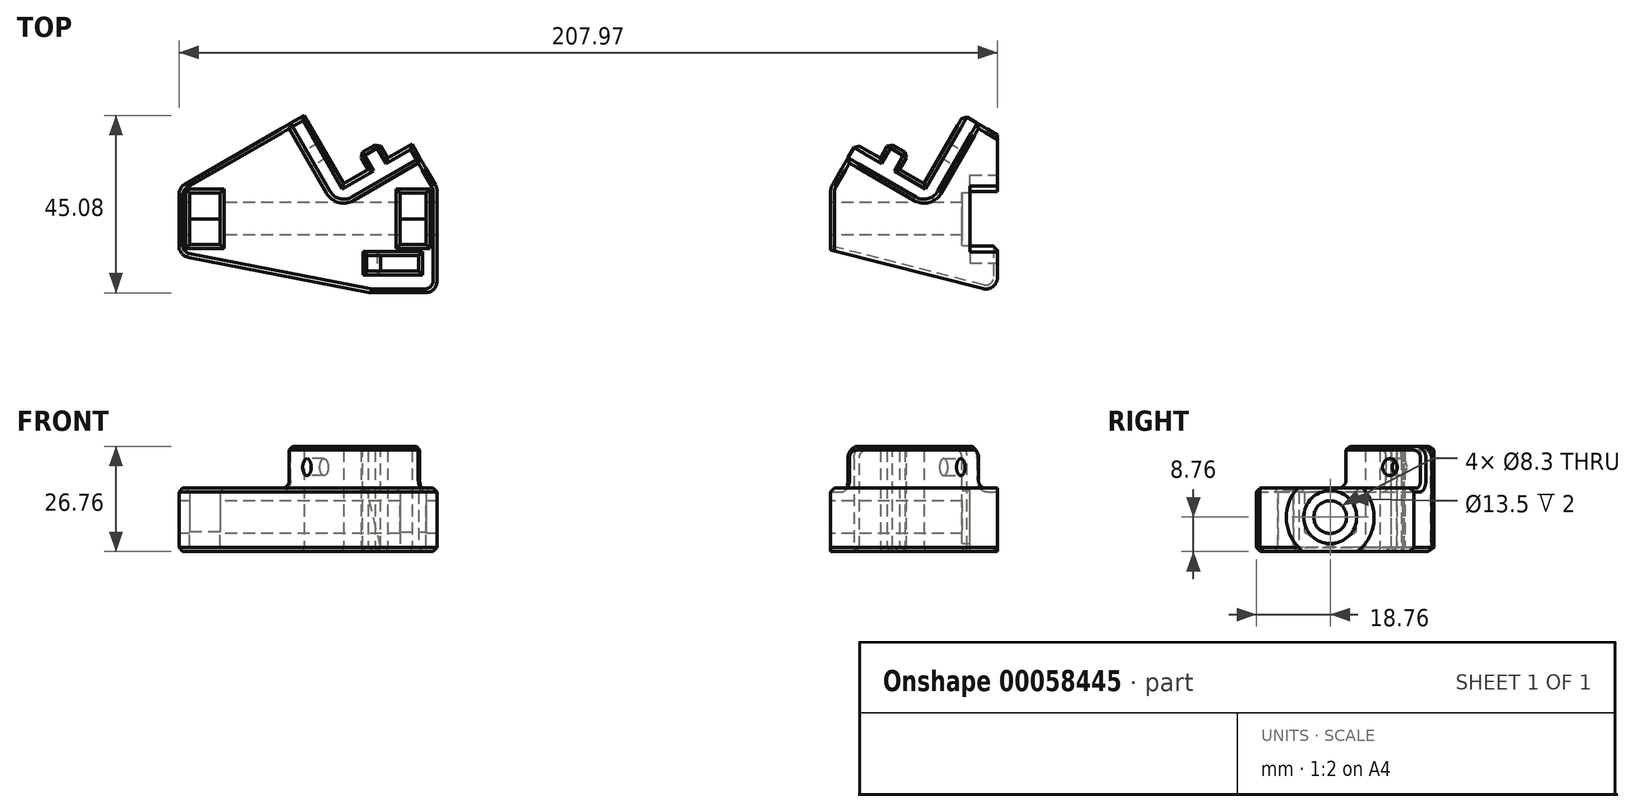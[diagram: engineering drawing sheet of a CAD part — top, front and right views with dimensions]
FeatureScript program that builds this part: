
annotation { "Feature Type Name" : "Feature", "Feature Type Description" : "" }
export const myFeature = defineFeature(function(context is Context, id is Id, definition is map)
    precondition{}
    {
        {
            assignVariable(context, id + "F0", {"name" : "line_width", "anyValue" : 0.48});
        }
        {
            assignVariable(context, id + "F1", {"name" : "tolerance", "anyValue" : 0.3});
        }
        {
            assignVariable(context, id + "F2", {"name" : "min_wall", "anyValue" : 3 * getVariable(context, 'line_width') * 0.95});
        }
        {
            assignVariable(context, id + "F3", {"name" : "M8_nut", "anyValue" : 12.8});
        }
        {
            assignVariable(context, id + "F4", {"name" : "M8_nut_long", "anyValue" : getVariable(context, 'M8_nut') / cos(30 * degree)});
        }
        {
            assignVariable(context, id + "F5", {"name" : "M8_nut_thickness", "anyValue" : 6.4});
        }
        {
            assignVariable(context, id + "F6", {"name" : "caliper_thickness", "anyValue" : 3.7});
        }
        {
            var Q0;
            Q0=qCreatedBy(makeId("Top.planeOp"),FACE);
            var sketch = newSketch(context, id + "F7", { "sketchPlane" : qUnion([Q0])});
            skLineSegment(sketch, "E0", {"start": v(-10, 26.32) * mm, "end": v(0, 9) * mm});
            skLineSegment(sketch, "E1", {"start": v(0, 9) * mm, "end": v(6.2, 12.57) * mm});
            skLineSegment(sketch, "E2", {"start": v(6.2, 12.57) * mm, "end": v(3.94, 16.47) * mm});
            skLineSegment(sketch, "E3", {"start": v(3.94, 16.47) * mm, "end": v(8.88, 19.32) * mm});
            skLineSegment(sketch, "E4", {"start": v(8.88, 19.32) * mm, "end": v(11.13, 15.42) * mm});
            skLineSegment(sketch, "E5", {"start": v(11.13, 15.42) * mm, "end": v(17.32, 19) * mm});
            skLineSegment(sketch, "E6", {"start": v(-41.87, 0) * mm, "end": v(23.72, 0) * mm, "construction": true});
            skLineSegment(sketch, "E7", {"start": v(-41.87, 0) * mm, "end": v(-41.87, -9.29) * mm});
            skLineSegment(sketch, "E8", {"start": v(-41.87, -9.29) * mm, "end": v(23.72, -9.29) * mm, "construction": true});
            skLineSegment(sketch, "E9", {"start": v(23.72, -9.29) * mm, "end": v(23.72, 0) * mm});
            skLineSegment(sketch, "E10", {"start": v(23.72, 0) * mm, "end": v(23.72, 7.92) * mm});
            skLineSegment(sketch, "E11", {"start": v(23.72, 7.92) * mm, "end": v(19.82, 14.67) * mm});
            skLineSegment(sketch, "E12", {"start": v(-41.87, 0) * mm, "end": v(-41.87, 7.92) * mm});
            skLineSegment(sketch, "E13", {"start": v(-41.87, 7.92) * mm, "end": v(-14.33, 23.82) * mm});
            skLineSegment(sketch, "E14", {"start": v(-41.87, -4) * mm, "end": v(23.72, -4) * mm, "construction": true});
            skLineSegment(sketch, "E15.MirrorCS", {"start": v(-41.87, 4) * mm, "end": v(23.72, 4) * mm, "construction": true});
            skLineSegment(sketch, "E16.rect.bottom", {"start": v(-31.44, -6.55) * mm, "end": v(-39.14, -6.55) * mm});
            skLineSegment(sketch, "E16.rect.top", {"start": v(-31.44, 6.55) * mm, "end": v(-39.14, 6.55) * mm});
            skLineSegment(sketch, "E16.rect.left", {"start": v(-31.44, -6.55) * mm, "end": v(-31.44, 6.55) * mm});
            skLineSegment(sketch, "E16.rect.right", {"start": v(-39.14, -6.55) * mm, "end": v(-39.14, 6.55) * mm});
            skPoint(sketch, "E16.rect.middle", {"position": v(-35.29, 0) * mm});
            skLineSegment(sketch, "E17.rect.bottom", {"start": v(20.98, -6.55) * mm, "end": v(14.28, -6.55) * mm});
            skLineSegment(sketch, "E17.rect.top", {"start": v(20.98, 6.55) * mm, "end": v(14.28, 6.55) * mm});
            skLineSegment(sketch, "E17.rect.left", {"start": v(20.98, -6.55) * mm, "end": v(20.98, 6.55) * mm});
            skLineSegment(sketch, "E17.rect.right", {"start": v(14.28, -6.55) * mm, "end": v(14.28, 6.55) * mm});
            skPoint(sketch, "E17.rect.middle", {"position": v(17.63, 0) * mm});
            skLineSegment(sketch, "E18", {"start": v(-39.14, -6.55) * mm, "end": v(-41.87, -6.55) * mm, "construction": true});
            skLineSegment(sketch, "E19", {"start": v(20.98, -6.55) * mm, "end": v(23.72, -6.55) * mm, "construction": true});
            skLineSegment(sketch, "E20", {"start": v(19.82, 14.67) * mm, "end": v(2.5, 4.67) * mm});
            skLineSegment(sketch, "E21", {"start": v(-4.33, 6.5) * mm, "end": v(-14.33, 23.82) * mm});
            skLineSegment(sketch, "E22", {"start": v(-14.33, 23.82) * mm, "end": v(-10, 26.32) * mm});
            skLineSegment(sketch, "E23", {"start": v(19.82, 14.67) * mm, "end": v(17.32, 19) * mm});
            skPoint(sketch, "E24.visualSharp", {"position": v(-1.83, 2.17) * mm});
            skArc(sketch, "E24.filletArc", {"start": v(-4.33, 6.5) * mm, "mid": v(-1.3, 4.17) * mm, "end": v(2.5, 4.67) * mm});
            skLineSegment(sketch, "E25", {"start": v(23.72, -9.29) * mm, "end": v(23.72, -18.76) * mm});
            skLineSegment(sketch, "E26", {"start": v(23.72, -18.76) * mm, "end": v(6.61, -18.76) * mm});
            skLineSegment(sketch, "E27", {"start": v(6.61, -18.76) * mm, "end": v(-41.87, -9.29) * mm});
            skSolve(sketch);
        }
        {
            var Q0;
            Q0 = qSketchRegion(id + "F7", true);
            extrude(context, id + "F8", {"entities" : qUnion([Q0]), "depth" : (getVariable(context, 'M8_nut_long') / 2) * mm});
        }
        {
            var Q0;
            Q0=makeQuery(id+"F7.imprint","IMPRINT",FACE,{"disambiguationData":[TD([[makeQuery(id+"F7.imprint","IMPRINT",EDGE,{"derivedFrom":sQuery(id+"F7.wireOp",EDGE,"E0")}),-1.0]])]});
            extrude(context, id + "F9", {"entities" : qUnion([Q0]), "operationType" : NewBodyOperationType.ADD, "depth" : 18 * mm});
        }
        {
            var Q0;
            Q0=makeQuery(id+"F7.imprint","IMPRINT",FACE,{"disambiguationData":[TD([[makeQuery(id+"F7.imprint","IMPRINT",EDGE,{"derivedFrom":sQuery(id+"F7.wireOp",EDGE,"E16.rect.bottom")}),-1.0]])]});
            var Q1;
            Q1=makeQuery(id+"F7.imprint","IMPRINT",FACE,{"disambiguationData":[TD([[makeQuery(id+"F7.imprint","IMPRINT",EDGE,{"derivedFrom":sQuery(id+"F7.wireOp",EDGE,"E17.rect.bottom")}),-1.0]])]});
            var Q2;
            Q2=makeQuery(id+"F7.imprint","IMPRINT",FACE,{"disambiguationData":[TD([[makeQuery(id+"F7.imprint","IMPRINT",EDGE,{"derivedFrom":sQuery(id+"F7.wireOp",EDGE,"E0")}),-1.0]])]});
            var Q3;
            Q3=makeQuery(id+"F7.imprint","IMPRINT",FACE,{"disambiguationData":[TD([[makeQuery(id+"F7.imprint","IMPRINT",EDGE,{"derivedFrom":sQuery(id+"F7.wireOp",EDGE,"E7")}),1.0]])]});
            extrude(context, id + "F10", {"entities" : qUnion([Q0, Q1, Q2, Q3]), "operationType" : NewBodyOperationType.ADD, "oppositeDirection" : true, "depth" : (getVariable(context, 'M8_nut_long') / 2 + getVariable(context, 'min_wall')) * mm});
        }
        {
            var Q0;
            Q0=makeQuery(id+"F8.opExtrude","SWEPT_FACE",FACE,{"disambiguationData":[OSD([sQuery(id+"F7.wireOp",EDGE,"E16.rect.right")])]});
            var sketch = newSketch(context, id + "F11", { "sketchPlane" : qUnion([Q0])});
            skCircle(sketch, "E28.cCircle", {"center": v(0, 0) * mm, "radius": 6.55 * mm, "construction": true});
            skPoint(sketch, "E28.cCircle.perimeterSnap0", {"position": v(0, 0) * mm});
            skLineSegment(sketch, "E28.0", {"start": v(6.55, 3.78) * mm, "end": v(6.55, -3.78) * mm});
            skLineSegment(sketch, "E28.1", {"start": v(6.55, -3.78) * mm, "end": v(0, -7.56) * mm});
            skLineSegment(sketch, "E28.2", {"start": v(0, -7.56) * mm, "end": v(-6.55, -3.78) * mm});
            skLineSegment(sketch, "E28.3", {"start": v(-6.55, -3.78) * mm, "end": v(-6.55, 3.78) * mm});
            skLineSegment(sketch, "E28.4", {"start": v(-6.55, 3.78) * mm, "end": v(0, 7.56) * mm});
            skLineSegment(sketch, "E28.5", {"start": v(0, 7.56) * mm, "end": v(6.55, 3.78) * mm});
            skPoint(sketch, "E28.0.midPoint", {"position": v(6.55, 0) * mm});
            skPoint(sketch, "E28.0.midPoint.positionSnap0", {"position": v(0, 0) * mm});
            skSolve(sketch);
        }
        {
            var Q0;
            {var subQ0=sQuery(id+"F7.wireOp",EDGE,"E25");var subQ1=sQuery(id+"F7.wireOp",EDGE,"E10");var subQ2=sQuery(id+"F7.wireOp",EDGE,"E9");Q0=makeQuery(id+"F10.boolean.opBoolean","MERGE",FACE,{"derivedFrom":[makeQuery(id+"F8.opExtrude","SWEPT_FACE",FACE,{"disambiguationData":[OSD([subQ2,subQ1,subQ0])]}),makeQuery(id+"F10.opExtrude","SWEPT_FACE",FACE,{"disambiguationData":[OSD([subQ2,subQ1,subQ0])]})]});}
            cPlane(context, id + "F12", {"entities" : qUnion([Q0]), "cplaneType" : CPlaneType.OFFSET, "offset" : 50 * mm, "width" : 150 * mm, "height" : 150 * mm});
        }
        {
            var Q0;
            Q0 = qSketchRegion(id + "F11", true);
            var Q1;
            Q1=makeQuery(id+"F8.opExtrude","SWEPT_FACE",FACE,{"disambiguationData":[OSD([sQuery(id+"F7.wireOp",EDGE,"E16.rect.left")])]});
            extrude(context, id + "F13", {"entities" : qUnion([Q0]), "operationType" : NewBodyOperationType.REMOVE, "endBound" : BoundingType.UP_TO_SURFACE, "endBoundEntityFace" : qUnion([Q1]), "depth" : (6.4 + getVariable(context, 'tolerance')) * mm});
        }
        {
            var Q0;
            Q0=makeQuery(id+"F8.opExtrude","SWEPT_FACE",FACE,{"disambiguationData":[OSD([sQuery(id+"F7.wireOp",EDGE,"E17.rect.left")])]});
            var sketch = newSketch(context, id + "F14", { "sketchPlane" : qUnion([Q0])});
            skCircle(sketch, "E29.cCircle", {"center": v(0, 0) * mm, "radius": 6.55 * mm, "construction": true});
            skPoint(sketch, "E29.cCircle.perimeterSnap0", {"position": v(0, 0) * mm});
            skLineSegment(sketch, "E29.0", {"start": v(6.55, 3.78) * mm, "end": v(6.55, -3.78) * mm});
            skLineSegment(sketch, "E29.1", {"start": v(6.55, -3.78) * mm, "end": v(0, -7.56) * mm});
            skLineSegment(sketch, "E29.2", {"start": v(0, -7.56) * mm, "end": v(-6.55, -3.78) * mm});
            skLineSegment(sketch, "E29.3", {"start": v(-6.55, -3.78) * mm, "end": v(-6.55, 3.78) * mm});
            skLineSegment(sketch, "E29.4", {"start": v(-6.55, 3.78) * mm, "end": v(0, 7.56) * mm});
            skLineSegment(sketch, "E29.5", {"start": v(0, 7.56) * mm, "end": v(6.55, 3.78) * mm});
            skPoint(sketch, "E29.0.midPoint", {"position": v(6.55, 0) * mm});
            skPoint(sketch, "E29.0.midPoint.positionSnap0", {"position": v(0, 0) * mm});
            skSolve(sketch);
        }
        {
            var Q0;
            Q0 = qSketchRegion(id + "F14", true);
            var Q1;
            Q1=makeQuery(id+"F8.opExtrude","SWEPT_FACE",FACE,{"disambiguationData":[OSD([sQuery(id+"F7.wireOp",EDGE,"E17.rect.right")])]});
            extrude(context, id + "F15", {"entities" : qUnion([Q0]), "operationType" : NewBodyOperationType.REMOVE, "endBound" : BoundingType.UP_TO_SURFACE, "endBoundEntityFace" : qUnion([Q1]), "depth" : (getVariable(context, 'M8_nut_thickness') + getVariable(context, 'tolerance')) * mm});
        }
        {
            var Q0;
            {var subQ0=sQuery(id+"F7.wireOp",EDGE,"E12");var subQ1=sQuery(id+"F7.wireOp",EDGE,"E7");Q0=makeQuery(id+"F10.boolean.opBoolean","MERGE",FACE,{"derivedFrom":[makeQuery(id+"F8.opExtrude","SWEPT_FACE",FACE,{"disambiguationData":[OSD([subQ1,subQ0])]}),makeQuery(id+"F10.opExtrude","SWEPT_FACE",FACE,{"disambiguationData":[OSD([subQ1,subQ0])]})]});}
            var sketch = newSketch(context, id + "F16", { "sketchPlane" : qUnion([Q0])});
            skCircle(sketch, "E30", {"center": v(0, 0) * mm, "radius": 4.15 * mm});
            skSolve(sketch);
        }
        {
            var Q0;
            {var subQ0=sQuery(id+"F7.wireOp",EDGE,"E22");var subQ4=sQuery(id+"F7.wireOp",EDGE,"E21");Q0=makeQuery(id+"F9.boolean.opBoolean","SPLIT",FACE,{"disambiguationData":[TD([makeQuery(id+"F9.opExtrude","SWEPT_FACE",FACE,{"disambiguationData":[OSD([subQ0])]})])],"derivedFrom":makeQuery(id+"F9.opExtrude","SWEPT_FACE",FACE,{"disambiguationData":[OSD([subQ4])]})});}
            var sketch = newSketch(context, id + "F17", { "sketchPlane" : qUnion([Q0])});
            skCircle(sketch, "E31", {"center": v(-17.8, 12.7) * mm, "radius": 2.15 * mm});
            skPoint(sketch, "E31.centerSnap0", {"position": v(-17.8, 18) * mm});
            skPoint(sketch, "E31.centerSnap1", {"position": v(-27.8, 12.7) * mm});
            skSolve(sketch);
        }
        {
            var Q0;
            Q0=makeQuery(id+"F17.imprint","IMPRINT",FACE,{"disambiguationData":[TD([[makeQuery(id+"F17.imprint","IMPRINT",EDGE,{"derivedFrom":sQuery(id+"F17.wireOp",EDGE,"E31")}),1.0]])]});
            var Q1;
            {var subQ0=sQuery(id+"F7.wireOp",EDGE,"E0");Q1=makeQuery(id+"F9.boolean.opBoolean","MERGE",FACE,{"derivedFrom":[makeQuery(id+"F10.boolean.opBoolean","MERGE",FACE,{"derivedFrom":[makeQuery(id+"F8.opExtrude","SWEPT_FACE",FACE,{"disambiguationData":[OSD([subQ0])]}),makeQuery(id+"F10.opExtrude","SWEPT_FACE",FACE,{"disambiguationData":[OSD([subQ0])]})]}),makeQuery(id+"F9.opExtrude","SWEPT_FACE",FACE,{"disambiguationData":[OSD([subQ0])]})]});}
            extrude(context, id + "F18", {"entities" : qUnion([Q0]), "operationType" : NewBodyOperationType.REMOVE, "endBound" : BoundingType.UP_TO_SURFACE, "oppositeDirection" : true, "endBoundEntityFace" : qUnion([Q1]), "depth" : 25 * mm});
        }
        {
            var Q0;
            Q0=makeQuery(id+"F8.opExtrude","SWEPT_BODY",BODY,{"disambiguationData":[OSD([sQuery(id+"F7.wireOp",EDGE,"E0"),sQuery(id+"F7.wireOp",EDGE,"E1"),sQuery(id+"F7.wireOp",EDGE,"E2"),sQuery(id+"F7.wireOp",EDGE,"E3"),sQuery(id+"F7.wireOp",EDGE,"E4"),sQuery(id+"F7.wireOp",EDGE,"E5"),sQuery(id+"F7.wireOp",EDGE,"E7"),sQuery(id+"F7.wireOp",EDGE,"E9"),sQuery(id+"F7.wireOp",EDGE,"E10"),sQuery(id+"F7.wireOp",EDGE,"E11"),sQuery(id+"F7.wireOp",EDGE,"E12"),sQuery(id+"F7.wireOp",EDGE,"E13"),sQuery(id+"F7.wireOp",EDGE,"E16.rect.bottom"),sQuery(id+"F7.wireOp",EDGE,"E16.rect.top"),sQuery(id+"F7.wireOp",EDGE,"E16.rect.left"),sQuery(id+"F7.wireOp",EDGE,"E16.rect.right"),sQuery(id+"F7.wireOp",EDGE,"E17.rect.bottom"),sQuery(id+"F7.wireOp",EDGE,"E17.rect.top"),sQuery(id+"F7.wireOp",EDGE,"E17.rect.left"),sQuery(id+"F7.wireOp",EDGE,"E17.rect.right"),sQuery(id+"F7.wireOp",EDGE,"E22"),sQuery(id+"F7.wireOp",EDGE,"E23"),sQuery(id+"F7.wireOp",EDGE,"E25"),sQuery(id+"F7.wireOp",EDGE,"E26"),sQuery(id+"F7.wireOp",EDGE,"E27")])]});
            var Q1;
            Q1=qCreatedBy(id+"F12.planeOp",FACE);
            mirror(context, id + "F19", {"entities" : qUnion([Q0]), "mirrorPlane" : qUnion([Q1])});
        }
        {
            var Q0;
            Q0=makeQuery(id+"F15.boolean.opBoolean","MERGE",FACE,{"derivedFrom":[makeQuery(id+"F8.opExtrude","SWEPT_FACE",FACE,{"disambiguationData":[OSD([sQuery(id+"F7.wireOp",EDGE,"E17.rect.bottom")])]}),makeQuery(id+"F15.opExtrude","SWEPT_FACE",FACE,{"disambiguationData":[OSD([sQuery(id+"F14.wireOp",EDGE,"E29.0")])]})]});
            cPlane(context, id + "F20", {"entities" : qUnion([Q0]), "cplaneType" : CPlaneType.OFFSET, "offset" : (getVariable(context, 'min_wall') * 2) * mm, "oppositeDirection" : true, "width" : 150 * mm, "height" : 150 * mm});
        }
        {
            var Q0;
            Q0=qCreatedBy(id+"F20.planeOp",FACE);
            var sketch = newSketch(context, id + "F21", { "sketchPlane" : qUnion([Q0])});
            skLineSegment(sketch, "E32.0", {"start": v(-20.98, 7.4) * mm, "end": v(-20.98, -3.78) * mm, "construction": true});
            skLineSegment(sketch, "E33", {"start": v(-18.98, 7.4) * mm, "end": v(-18.98, -8.76) * mm});
            skLineSegment(sketch, "E34", {"start": v(-18.98, -8.76) * mm, "end": v(-9.7, -8.76) * mm});
            skLineSegment(sketch, "E35", {"start": v(-9.7, -8.76) * mm, "end": v(-5.68, 7.4) * mm});
            skLineSegment(sketch, "E36", {"start": v(-5.68, 7.4) * mm, "end": v(-18.98, 7.4) * mm});
            skSolve(sketch);
        }
        {
            var Q0;
            Q0=makeQuery(id+"F21.imprint","IMPRINT",FACE,{"disambiguationData":[TD([[makeQuery(id+"F21.imprint","IMPRINT",EDGE,{"derivedFrom":sQuery(id+"F21.wireOp",EDGE,"E33")}),1.0]])]});
            extrude(context, id + "F22", {"entities" : qUnion([Q0]), "operationType" : NewBodyOperationType.REMOVE, "oppositeDirection" : true, "depth" : (getVariable(context, 'caliper_thickness') + getVariable(context, 'tolerance')) * mm});
        }
        {
            var Q0;
            Q0=makeQuery(id+"F19.opPattern","COPY",FACE,{"derivedFrom":makeQuery(id+"F10.opExtrude","CAP_FACE",FACE,{"disambiguationData":[OSD([sQuery(id+"F7.wireOp",EDGE,"E0"),sQuery(id+"F7.wireOp",EDGE,"E1"),sQuery(id+"F7.wireOp",EDGE,"E2"),sQuery(id+"F7.wireOp",EDGE,"E3"),sQuery(id+"F7.wireOp",EDGE,"E4"),sQuery(id+"F7.wireOp",EDGE,"E5"),sQuery(id+"F7.wireOp",EDGE,"E7"),sQuery(id+"F7.wireOp",EDGE,"E9"),sQuery(id+"F7.wireOp",EDGE,"E10"),sQuery(id+"F7.wireOp",EDGE,"E11"),sQuery(id+"F7.wireOp",EDGE,"E12"),sQuery(id+"F7.wireOp",EDGE,"E13"),sQuery(id+"F7.wireOp",EDGE,"E22"),sQuery(id+"F7.wireOp",EDGE,"E23"),sQuery(id+"F7.wireOp",EDGE,"E25"),sQuery(id+"F7.wireOp",EDGE,"E26"),sQuery(id+"F7.wireOp",EDGE,"E27")])],"isStart":false}),"instanceName":"1"});
            var sketch = newSketch(context, id + "F23", { "sketchPlane" : qUnion([Q0])});
            skLineSegment(sketch, "E37", {"start": v(123.72, 7.92) * mm, "end": v(166.1, 18.68) * mm});
            skLineSegment(sketch, "E38", {"start": v(166.1, 18.68) * mm, "end": v(166.1, -21.32) * mm});
            skSolve(sketch);
        }
        {
            var Q0;
            {var subQ5=sQuery(id+"F23.wireOp",EDGE,"E37");Q0=makeQuery(id+"F23.imprint","IMPRINT",FACE,{"disambiguationData":[TD([[makeQuery(id+"F23.imprint","IMPRINT",EDGE,{"derivedFrom":subQ5}),1.0]])]});}
            var Q1;
            {var subQ5=makeQuery(id+"F19.opPattern","COPY",EDGE,{"derivedFrom":makeQuery(id+"F10.opExtrude","CAP_EDGE",EDGE,{"disambiguationData":[OSD([sQuery(id+"F7.wireOp",EDGE,"E7"),sQuery(id+"F7.wireOp",EDGE,"E12")])],"isStart":false}),"instanceName":"1"});Q1=makeQuery(id+"F23.imprint","IMPRINT",FACE,{"disambiguationData":[TD([[makeQuery(id+"F23.imprint","IMPRINT",EDGE,{"derivedFrom":subQ5}),-1.0]])]});}
            var Q2;
            Q2=makeQuery(id+"F19.opPattern","COPY",FACE,{"derivedFrom":makeQuery(id+"F8.opExtrude","CAP_FACE",FACE,{"disambiguationData":[OSD([sQuery(id+"F7.wireOp",EDGE,"E0"),sQuery(id+"F7.wireOp",EDGE,"E1"),sQuery(id+"F7.wireOp",EDGE,"E2"),sQuery(id+"F7.wireOp",EDGE,"E3"),sQuery(id+"F7.wireOp",EDGE,"E4"),sQuery(id+"F7.wireOp",EDGE,"E5"),sQuery(id+"F7.wireOp",EDGE,"E7"),sQuery(id+"F7.wireOp",EDGE,"E9"),sQuery(id+"F7.wireOp",EDGE,"E10"),sQuery(id+"F7.wireOp",EDGE,"E11"),sQuery(id+"F7.wireOp",EDGE,"E12"),sQuery(id+"F7.wireOp",EDGE,"E13"),sQuery(id+"F7.wireOp",EDGE,"E16.rect.bottom"),sQuery(id+"F7.wireOp",EDGE,"E16.rect.top"),sQuery(id+"F7.wireOp",EDGE,"E16.rect.left"),sQuery(id+"F7.wireOp",EDGE,"E16.rect.right"),sQuery(id+"F7.wireOp",EDGE,"E17.rect.bottom"),sQuery(id+"F7.wireOp",EDGE,"E17.rect.top"),sQuery(id+"F7.wireOp",EDGE,"E17.rect.left"),sQuery(id+"F7.wireOp",EDGE,"E17.rect.right"),sQuery(id+"F7.wireOp",EDGE,"E22"),sQuery(id+"F7.wireOp",EDGE,"E23"),sQuery(id+"F7.wireOp",EDGE,"E25"),sQuery(id+"F7.wireOp",EDGE,"E26"),sQuery(id+"F7.wireOp",EDGE,"E27")])],"isStart":false}),"instanceName":"1"});
            extrude(context, id + "F24", {"entities" : qUnion([Q0, Q1]), "operationType" : NewBodyOperationType.REMOVE, "endBound" : BoundingType.UP_TO_SURFACE, "oppositeDirection" : true, "endBoundEntityFace" : qUnion([Q2]), "depth" : 25 * mm});
        }
        {
            var Q0;
            Q0=makeQuery(id+"F19.opPattern","COPY",FACE,{"derivedFrom":makeQuery(id+"F10.opExtrude","CAP_FACE",FACE,{"disambiguationData":[OSD([sQuery(id+"F7.wireOp",EDGE,"E0"),sQuery(id+"F7.wireOp",EDGE,"E1"),sQuery(id+"F7.wireOp",EDGE,"E2"),sQuery(id+"F7.wireOp",EDGE,"E3"),sQuery(id+"F7.wireOp",EDGE,"E4"),sQuery(id+"F7.wireOp",EDGE,"E5"),sQuery(id+"F7.wireOp",EDGE,"E7"),sQuery(id+"F7.wireOp",EDGE,"E9"),sQuery(id+"F7.wireOp",EDGE,"E10"),sQuery(id+"F7.wireOp",EDGE,"E11"),sQuery(id+"F7.wireOp",EDGE,"E12"),sQuery(id+"F7.wireOp",EDGE,"E13"),sQuery(id+"F7.wireOp",EDGE,"E22"),sQuery(id+"F7.wireOp",EDGE,"E23"),sQuery(id+"F7.wireOp",EDGE,"E25"),sQuery(id+"F7.wireOp",EDGE,"E26"),sQuery(id+"F7.wireOp",EDGE,"E27")])],"isStart":false}),"instanceName":"1"});
            var Q1;
            {var subQ0=sQuery(id+"F23.wireOp",EDGE,"E38");var subQ1=sQuery(id+"F23.wireOp",EDGE,"E37");var subQ2=makeQuery(id+"F23.imprint","INTERSECT",VERTEX,{"derivedFrom":[subQ1,subQ0]});Q1=makeQuery(id+"F23.imprint","IMPRINT",FACE,{"disambiguationData":[TD([[makeQuery(id+"F23.imprint","IMPRINT",EDGE,{"disambiguationData":[TD([[subQ2,1.0]])],"derivedFrom":subQ1}),-1.0]])]});}
            var Q2;
            Q2=makeQuery(id+"F19.opPattern","COPY",FACE,{"derivedFrom":makeQuery(id+"F8.opExtrude","CAP_FACE",FACE,{"disambiguationData":[OSD([sQuery(id+"F7.wireOp",EDGE,"E0"),sQuery(id+"F7.wireOp",EDGE,"E1"),sQuery(id+"F7.wireOp",EDGE,"E2"),sQuery(id+"F7.wireOp",EDGE,"E3"),sQuery(id+"F7.wireOp",EDGE,"E4"),sQuery(id+"F7.wireOp",EDGE,"E5"),sQuery(id+"F7.wireOp",EDGE,"E7"),sQuery(id+"F7.wireOp",EDGE,"E9"),sQuery(id+"F7.wireOp",EDGE,"E10"),sQuery(id+"F7.wireOp",EDGE,"E11"),sQuery(id+"F7.wireOp",EDGE,"E12"),sQuery(id+"F7.wireOp",EDGE,"E13"),sQuery(id+"F7.wireOp",EDGE,"E16.rect.bottom"),sQuery(id+"F7.wireOp",EDGE,"E16.rect.top"),sQuery(id+"F7.wireOp",EDGE,"E16.rect.left"),sQuery(id+"F7.wireOp",EDGE,"E16.rect.right"),sQuery(id+"F7.wireOp",EDGE,"E17.rect.bottom"),sQuery(id+"F7.wireOp",EDGE,"E17.rect.top"),sQuery(id+"F7.wireOp",EDGE,"E17.rect.left"),sQuery(id+"F7.wireOp",EDGE,"E17.rect.right"),sQuery(id+"F7.wireOp",EDGE,"E22"),sQuery(id+"F7.wireOp",EDGE,"E23"),sQuery(id+"F7.wireOp",EDGE,"E25"),sQuery(id+"F7.wireOp",EDGE,"E26"),sQuery(id+"F7.wireOp",EDGE,"E27")])],"isStart":false}),"instanceName":"1"});
            extrude(context, id + "F25", {"entities" : qUnion([Q0, Q1]), "operationType" : NewBodyOperationType.ADD, "endBound" : BoundingType.UP_TO_SURFACE, "oppositeDirection" : true, "endBoundEntityFace" : qUnion([Q2]), "depth" : 25 * mm});
        }
        {
            var Q0;
            Q0=makeQuery(id+"F16.imprint","IMPRINT",FACE,{"disambiguationData":[TD([[makeQuery(id+"F16.imprint","IMPRINT",EDGE,{"derivedFrom":sQuery(id+"F16.wireOp",EDGE,"E30")}),1.0]])]});
            var Q1;
            {var subQ0=sQuery(id+"F23.wireOp",EDGE,"E38");Q1=makeQuery(id+"F25.boolean.opBoolean","MERGE",FACE,{"derivedFrom":[makeQuery(id+"F24.boolean.opBoolean","COPY",FACE,{"derivedFrom":makeQuery(id+"F24.opExtrude","SWEPT_FACE",FACE,{"disambiguationData":[OSD([subQ0])]})}),makeQuery(id+"F25.opExtrude","SWEPT_FACE",FACE,{"disambiguationData":[OSD([subQ0]),TDD([makeQuery(id+"F23.imprint","IMPRINT",EDGE,{"disambiguationData":[TD([[makeQuery(id+"F23.imprint","INTERSECT",VERTEX,{"derivedFrom":[sQuery(id+"F23.wireOp",EDGE,"E37"),subQ0]}),-1.0]])],"derivedFrom":subQ0})])]}),makeQuery(id+"F25.opExtrude","SWEPT_FACE",FACE,{"disambiguationData":[OSD([subQ0]),TDD([makeQuery(id+"F24.boolean.opBoolean","COPY",EDGE,{"derivedFrom":makeQuery(id+"F24.opExtrude","CAP_EDGE",EDGE,{"disambiguationData":[OSD([subQ0])],"isStart":true})})])]})]});}
            extrude(context, id + "F26", {"entities" : qUnion([Q0]), "operationType" : NewBodyOperationType.REMOVE, "endBound" : BoundingType.UP_TO_SURFACE, "oppositeDirection" : true, "endBoundEntityFace" : qUnion([Q1]), "depth" : 25 * mm});
        }
        {
            var Q0;
            {var subQ0=sQuery(id+"F23.wireOp",EDGE,"E38");Q0=makeQuery(id+"F25.boolean.opBoolean","MERGE",FACE,{"derivedFrom":[makeQuery(id+"F24.boolean.opBoolean","COPY",FACE,{"derivedFrom":makeQuery(id+"F24.opExtrude","SWEPT_FACE",FACE,{"disambiguationData":[OSD([subQ0])]})}),makeQuery(id+"F25.opExtrude","SWEPT_FACE",FACE,{"disambiguationData":[OSD([subQ0]),TDD([makeQuery(id+"F23.imprint","IMPRINT",EDGE,{"disambiguationData":[TD([[makeQuery(id+"F23.imprint","INTERSECT",VERTEX,{"derivedFrom":[sQuery(id+"F23.wireOp",EDGE,"E37"),subQ0]}),-1.0]])],"derivedFrom":subQ0})])]}),makeQuery(id+"F25.opExtrude","SWEPT_FACE",FACE,{"disambiguationData":[OSD([subQ0]),TDD([makeQuery(id+"F24.boolean.opBoolean","COPY",EDGE,{"derivedFrom":makeQuery(id+"F24.opExtrude","CAP_EDGE",EDGE,{"disambiguationData":[OSD([subQ0])],"isStart":true})})])]})]});}
            var sketch = newSketch(context, id + "F27", { "sketchPlane" : qUnion([Q0])});
            skCircle(sketch, "E39", {"center": v(0, 0) * mm, "radius": 11.15 * mm});
            skCircle(sketch, "E40", {"center": v(0, 0) * mm, "radius": 6.75 * mm});
            skSolve(sketch);
        }
        {
            var Q0;
            Q0=makeQuery(id+"F27.imprint","IMPRINT",FACE,{"disambiguationData":[TD([[makeQuery(id+"F27.imprint","IMPRINT",EDGE,{"derivedFrom":sQuery(id+"F27.wireOp",EDGE,"E40")}),-1.0]])]});
            extrude(context, id + "F28", {"entities" : qUnion([Q0]), "operationType" : NewBodyOperationType.REMOVE, "oppositeDirection" : true, "depth" : 7 * mm});
        }
        {
            var Q0;
            {var subQ0=sQuery(id+"F23.wireOp",EDGE,"E38");Q0=makeQuery(id+"F28.boolean.opBoolean","SPLIT",FACE,{"disambiguationData":[TD([makeQuery(id+"F26.boolean.opBoolean","COPY",FACE,{"disambiguationData":[OD(1.0)],"derivedFrom":makeQuery(id+"F26.opExtrude","SWEPT_FACE",FACE,{"disambiguationData":[OSD([sQuery(id+"F16.wireOp",EDGE,"E30")])]})})])],"derivedFrom":makeQuery(id+"F25.boolean.opBoolean","MERGE",FACE,{"derivedFrom":[makeQuery(id+"F24.boolean.opBoolean","COPY",FACE,{"derivedFrom":makeQuery(id+"F24.opExtrude","SWEPT_FACE",FACE,{"disambiguationData":[OSD([subQ0])]})}),makeQuery(id+"F25.opExtrude","SWEPT_FACE",FACE,{"disambiguationData":[OSD([subQ0]),TDD([makeQuery(id+"F23.imprint","IMPRINT",EDGE,{"disambiguationData":[TD([[makeQuery(id+"F23.imprint","INTERSECT",VERTEX,{"derivedFrom":[sQuery(id+"F23.wireOp",EDGE,"E37"),subQ0]}),-1.0]])],"derivedFrom":subQ0})])]}),makeQuery(id+"F25.opExtrude","SWEPT_FACE",FACE,{"disambiguationData":[OSD([subQ0]),TDD([makeQuery(id+"F24.boolean.opBoolean","COPY",EDGE,{"derivedFrom":makeQuery(id+"F24.opExtrude","CAP_EDGE",EDGE,{"disambiguationData":[OSD([subQ0])],"isStart":true})})])]})]})});}
            extrude(context, id + "F29", {"entities" : qUnion([Q0]), "operationType" : NewBodyOperationType.REMOVE, "oppositeDirection" : true, "depth" : 9 * mm});
        }
        {
            var Q0;
            Q0=makeQuery(id+"F9.boolean.opBoolean","INTERSECT",EDGE,{"derivedFrom":[makeQuery(id+"F8.opExtrude","CAP_FACE",FACE,{"disambiguationData":[OSD([sQuery(id+"F7.wireOp",EDGE,"E0"),sQuery(id+"F7.wireOp",EDGE,"E1"),sQuery(id+"F7.wireOp",EDGE,"E2"),sQuery(id+"F7.wireOp",EDGE,"E3"),sQuery(id+"F7.wireOp",EDGE,"E4"),sQuery(id+"F7.wireOp",EDGE,"E5"),sQuery(id+"F7.wireOp",EDGE,"E7"),sQuery(id+"F7.wireOp",EDGE,"E9"),sQuery(id+"F7.wireOp",EDGE,"E10"),sQuery(id+"F7.wireOp",EDGE,"E11"),sQuery(id+"F7.wireOp",EDGE,"E12"),sQuery(id+"F7.wireOp",EDGE,"E13"),sQuery(id+"F7.wireOp",EDGE,"E16.rect.bottom"),sQuery(id+"F7.wireOp",EDGE,"E16.rect.top"),sQuery(id+"F7.wireOp",EDGE,"E16.rect.left"),sQuery(id+"F7.wireOp",EDGE,"E16.rect.right"),sQuery(id+"F7.wireOp",EDGE,"E17.rect.bottom"),sQuery(id+"F7.wireOp",EDGE,"E17.rect.top"),sQuery(id+"F7.wireOp",EDGE,"E17.rect.left"),sQuery(id+"F7.wireOp",EDGE,"E17.rect.right"),sQuery(id+"F7.wireOp",EDGE,"E22"),sQuery(id+"F7.wireOp",EDGE,"E23"),sQuery(id+"F7.wireOp",EDGE,"E25"),sQuery(id+"F7.wireOp",EDGE,"E26"),sQuery(id+"F7.wireOp",EDGE,"E27")])],"isStart":false}),makeQuery(id+"F9.opExtrude","SWEPT_FACE",FACE,{"disambiguationData":[OSD([sQuery(id+"F7.wireOp",EDGE,"E21")])]})]});
            var Q1;
            Q1=makeQuery(id+"F19.opPattern","COPY",EDGE,{"derivedFrom":makeQuery(id+"F9.boolean.opBoolean","INTERSECT",EDGE,{"derivedFrom":[makeQuery(id+"F8.opExtrude","CAP_FACE",FACE,{"disambiguationData":[OSD([sQuery(id+"F7.wireOp",EDGE,"E0"),sQuery(id+"F7.wireOp",EDGE,"E1"),sQuery(id+"F7.wireOp",EDGE,"E2"),sQuery(id+"F7.wireOp",EDGE,"E3"),sQuery(id+"F7.wireOp",EDGE,"E4"),sQuery(id+"F7.wireOp",EDGE,"E5"),sQuery(id+"F7.wireOp",EDGE,"E7"),sQuery(id+"F7.wireOp",EDGE,"E9"),sQuery(id+"F7.wireOp",EDGE,"E10"),sQuery(id+"F7.wireOp",EDGE,"E11"),sQuery(id+"F7.wireOp",EDGE,"E12"),sQuery(id+"F7.wireOp",EDGE,"E13"),sQuery(id+"F7.wireOp",EDGE,"E16.rect.bottom"),sQuery(id+"F7.wireOp",EDGE,"E16.rect.top"),sQuery(id+"F7.wireOp",EDGE,"E16.rect.left"),sQuery(id+"F7.wireOp",EDGE,"E16.rect.right"),sQuery(id+"F7.wireOp",EDGE,"E17.rect.bottom"),sQuery(id+"F7.wireOp",EDGE,"E17.rect.top"),sQuery(id+"F7.wireOp",EDGE,"E17.rect.left"),sQuery(id+"F7.wireOp",EDGE,"E17.rect.right"),sQuery(id+"F7.wireOp",EDGE,"E22"),sQuery(id+"F7.wireOp",EDGE,"E23"),sQuery(id+"F7.wireOp",EDGE,"E25"),sQuery(id+"F7.wireOp",EDGE,"E26"),sQuery(id+"F7.wireOp",EDGE,"E27")])],"isStart":false}),makeQuery(id+"F9.opExtrude","SWEPT_FACE",FACE,{"disambiguationData":[OSD([sQuery(id+"F7.wireOp",EDGE,"E20")])]})]}),"instanceName":"1"});
            fillet(context, id + "F30", {"entities" : qUnion([Q0, Q1]), "radius" : 2 * mm, "tangentPropagation" : true, "allowEdgeOverflow" : false});
        }
        {
            var Q0;
            Q0=makeQuery(id+"F19.opPattern","COPY",EDGE,{"derivedFrom":makeQuery(id+"F9.opExtrude","CAP_EDGE",EDGE,{"disambiguationData":[OSD([sQuery(id+"F7.wireOp",EDGE,"E22")])],"isStart":false}),"instanceName":"1"});
            var Q1;
            Q1=makeQuery(id+"F19.opPattern","COPY",EDGE,{"derivedFrom":makeQuery(id+"F9.opExtrude","CAP_EDGE",EDGE,{"disambiguationData":[OSD([sQuery(id+"F7.wireOp",EDGE,"E23")])],"isStart":false}),"instanceName":"1"});
            var Q2;
            Q2=makeQuery(id+"F24.boolean.opBoolean","COPY",EDGE,{"derivedFrom":makeQuery(id+"F24.opExtrude","SWEPT_EDGE",EDGE,{"disambiguationData":[OSD([sQuery(id+"F7.wireOp",EDGE,"E13"),sQuery(id+"F7.wireOp",EDGE,"E22"),sQuery(id+"F23.wireOp",EDGE,"E38")])]})});
            var Q3;
            Q3=makeQuery(id+"F25.opExtrude","SWEPT_EDGE",EDGE,{"disambiguationData":[OSD([sQuery(id+"F23.wireOp",EDGE,"E37"),sQuery(id+"F23.wireOp",EDGE,"E38")])]});
            var Q4;
            Q4=makeQuery(id+"F24.boolean.opBoolean","COPY",EDGE,{"derivedFrom":makeQuery(id+"F24.opExtrude","SWEPT_EDGE",EDGE,{"disambiguationData":[OSD([sQuery(id+"F7.wireOp",EDGE,"E9"),sQuery(id+"F7.wireOp",EDGE,"E10"),sQuery(id+"F7.wireOp",EDGE,"E25"),sQuery(id+"F23.wireOp",EDGE,"E37")])]})});
            var Q5;
            {var subQ0=sQuery(id+"F7.wireOp",EDGE,"E11");var subQ1=sQuery(id+"F7.wireOp",EDGE,"E10");Q5=makeQuery(id+"F19.opPattern","COPY",EDGE,{"derivedFrom":makeQuery(id+"F10.boolean.opBoolean","MERGE",EDGE,{"derivedFrom":[makeQuery(id+"F8.opExtrude","SWEPT_EDGE",EDGE,{"disambiguationData":[OSD([subQ1,subQ0])]}),makeQuery(id+"F10.opExtrude","SWEPT_EDGE",EDGE,{"disambiguationData":[OSD([subQ1,subQ0])]})]}),"instanceName":"1"});}
            var Q6;
            {var subQ0=sQuery(id+"F7.wireOp",EDGE,"E26");var subQ1=sQuery(id+"F7.wireOp",EDGE,"E25");Q6=makeQuery(id+"F10.boolean.opBoolean","MERGE",EDGE,{"derivedFrom":[makeQuery(id+"F8.opExtrude","SWEPT_EDGE",EDGE,{"disambiguationData":[OSD([subQ1,subQ0])]}),makeQuery(id+"F10.opExtrude","SWEPT_EDGE",EDGE,{"disambiguationData":[OSD([subQ1,subQ0])]})]});}
            var Q7;
            {var subQ0=sQuery(id+"F7.wireOp",EDGE,"E27");var subQ1=sQuery(id+"F7.wireOp",EDGE,"E26");Q7=makeQuery(id+"F10.boolean.opBoolean","MERGE",EDGE,{"derivedFrom":[makeQuery(id+"F8.opExtrude","SWEPT_EDGE",EDGE,{"disambiguationData":[OSD([subQ1,subQ0])]}),makeQuery(id+"F10.opExtrude","SWEPT_EDGE",EDGE,{"disambiguationData":[OSD([subQ1,subQ0])]})]});}
            var Q8;
            {var subQ0=sQuery(id+"F7.wireOp",EDGE,"E27");var subQ1=sQuery(id+"F7.wireOp",EDGE,"E7");Q8=makeQuery(id+"F10.boolean.opBoolean","MERGE",EDGE,{"derivedFrom":[makeQuery(id+"F8.opExtrude","SWEPT_EDGE",EDGE,{"disambiguationData":[OSD([subQ1,subQ0])]}),makeQuery(id+"F10.opExtrude","SWEPT_EDGE",EDGE,{"disambiguationData":[OSD([subQ1,subQ0])]})]});}
            var Q9;
            {var subQ0=sQuery(id+"F7.wireOp",EDGE,"E13");var subQ1=sQuery(id+"F7.wireOp",EDGE,"E12");Q9=makeQuery(id+"F10.boolean.opBoolean","MERGE",EDGE,{"derivedFrom":[makeQuery(id+"F8.opExtrude","SWEPT_EDGE",EDGE,{"disambiguationData":[OSD([subQ1,subQ0])]}),makeQuery(id+"F10.opExtrude","SWEPT_EDGE",EDGE,{"disambiguationData":[OSD([subQ1,subQ0])]})]});}
            var Q10;
            {var subQ0=sQuery(id+"F7.wireOp",EDGE,"E11");var subQ1=sQuery(id+"F7.wireOp",EDGE,"E10");Q10=makeQuery(id+"F10.boolean.opBoolean","MERGE",EDGE,{"derivedFrom":[makeQuery(id+"F8.opExtrude","SWEPT_EDGE",EDGE,{"disambiguationData":[OSD([subQ1,subQ0])]}),makeQuery(id+"F10.opExtrude","SWEPT_EDGE",EDGE,{"disambiguationData":[OSD([subQ1,subQ0])]})]});}
            fillet(context, id + "F31", {"entities" : qUnion([Q0, Q1, Q2, Q3, Q4, Q5, Q6, Q7, Q8, Q9, Q10]), "radius" : 3 * mm, "tangentPropagation" : true, "allowEdgeOverflow" : false});
        }
        {
            var Q0;
            Q0=makeQuery(id+"F8.opExtrude","CAP_FACE",FACE,{"disambiguationData":[OSD([sQuery(id+"F7.wireOp",EDGE,"E0"),sQuery(id+"F7.wireOp",EDGE,"E1"),sQuery(id+"F7.wireOp",EDGE,"E2"),sQuery(id+"F7.wireOp",EDGE,"E3"),sQuery(id+"F7.wireOp",EDGE,"E4"),sQuery(id+"F7.wireOp",EDGE,"E5"),sQuery(id+"F7.wireOp",EDGE,"E7"),sQuery(id+"F7.wireOp",EDGE,"E9"),sQuery(id+"F7.wireOp",EDGE,"E10"),sQuery(id+"F7.wireOp",EDGE,"E11"),sQuery(id+"F7.wireOp",EDGE,"E12"),sQuery(id+"F7.wireOp",EDGE,"E13"),sQuery(id+"F7.wireOp",EDGE,"E16.rect.bottom"),sQuery(id+"F7.wireOp",EDGE,"E16.rect.top"),sQuery(id+"F7.wireOp",EDGE,"E16.rect.left"),sQuery(id+"F7.wireOp",EDGE,"E16.rect.right"),sQuery(id+"F7.wireOp",EDGE,"E17.rect.bottom"),sQuery(id+"F7.wireOp",EDGE,"E17.rect.top"),sQuery(id+"F7.wireOp",EDGE,"E17.rect.left"),sQuery(id+"F7.wireOp",EDGE,"E17.rect.right"),sQuery(id+"F7.wireOp",EDGE,"E22"),sQuery(id+"F7.wireOp",EDGE,"E23"),sQuery(id+"F7.wireOp",EDGE,"E25"),sQuery(id+"F7.wireOp",EDGE,"E26"),sQuery(id+"F7.wireOp",EDGE,"E27")])],"isStart":false});
            var Q1;
            Q1=makeQuery(id+"F10.opExtrude","CAP_FACE",FACE,{"disambiguationData":[OSD([sQuery(id+"F7.wireOp",EDGE,"E0"),sQuery(id+"F7.wireOp",EDGE,"E1"),sQuery(id+"F7.wireOp",EDGE,"E2"),sQuery(id+"F7.wireOp",EDGE,"E3"),sQuery(id+"F7.wireOp",EDGE,"E4"),sQuery(id+"F7.wireOp",EDGE,"E5"),sQuery(id+"F7.wireOp",EDGE,"E7"),sQuery(id+"F7.wireOp",EDGE,"E9"),sQuery(id+"F7.wireOp",EDGE,"E10"),sQuery(id+"F7.wireOp",EDGE,"E11"),sQuery(id+"F7.wireOp",EDGE,"E12"),sQuery(id+"F7.wireOp",EDGE,"E13"),sQuery(id+"F7.wireOp",EDGE,"E22"),sQuery(id+"F7.wireOp",EDGE,"E23"),sQuery(id+"F7.wireOp",EDGE,"E25"),sQuery(id+"F7.wireOp",EDGE,"E26"),sQuery(id+"F7.wireOp",EDGE,"E27")])],"isStart":false});
            var Q2;
            {var subQ0=sQuery(id+"F7.wireOp",EDGE,"E27");var subQ1=sQuery(id+"F7.wireOp",EDGE,"E25");var subQ2=sQuery(id+"F7.wireOp",EDGE,"E10");var subQ3=sQuery(id+"F7.wireOp",EDGE,"E9");var subQ4=makeQuery(id+"F19.opPattern","COPY",FACE,{"derivedFrom":makeQuery(id+"F8.opExtrude","CAP_FACE",FACE,{"disambiguationData":[OSD([sQuery(id+"F7.wireOp",EDGE,"E0"),sQuery(id+"F7.wireOp",EDGE,"E1"),sQuery(id+"F7.wireOp",EDGE,"E2"),sQuery(id+"F7.wireOp",EDGE,"E3"),sQuery(id+"F7.wireOp",EDGE,"E4"),sQuery(id+"F7.wireOp",EDGE,"E5"),sQuery(id+"F7.wireOp",EDGE,"E7"),subQ3,subQ2,sQuery(id+"F7.wireOp",EDGE,"E11"),sQuery(id+"F7.wireOp",EDGE,"E12"),sQuery(id+"F7.wireOp",EDGE,"E13"),sQuery(id+"F7.wireOp",EDGE,"E16.rect.bottom"),sQuery(id+"F7.wireOp",EDGE,"E16.rect.top"),sQuery(id+"F7.wireOp",EDGE,"E16.rect.left"),sQuery(id+"F7.wireOp",EDGE,"E16.rect.right"),sQuery(id+"F7.wireOp",EDGE,"E17.rect.bottom"),sQuery(id+"F7.wireOp",EDGE,"E17.rect.top"),sQuery(id+"F7.wireOp",EDGE,"E17.rect.left"),sQuery(id+"F7.wireOp",EDGE,"E17.rect.right"),sQuery(id+"F7.wireOp",EDGE,"E22"),sQuery(id+"F7.wireOp",EDGE,"E23"),subQ1,sQuery(id+"F7.wireOp",EDGE,"E26"),subQ0])],"isStart":false}),"instanceName":"1"});var subQ5=subQ4;var subQ6=sQuery(id+"F23.wireOp",EDGE,"E37");var subQ7=makeQuery(id+"F23.imprint","INTERSECT",VERTEX,{"derivedFrom":[makeQuery(id+"F19.opPattern","COPY",EDGE,{"derivedFrom":makeQuery(id+"F10.opExtrude","CAP_EDGE",EDGE,{"disambiguationData":[OSD([subQ0])],"isStart":false}),"instanceName":"1"}),subQ6]});Q2=makeQuery(id+"F25.boolean.opBoolean","MERGE",EDGE,{"derivedFrom":[makeQuery(id+"F24.boolean.opBoolean","COPY",EDGE,{"derivedFrom":makeQuery(id+"F24.opExtrude","TWEAK_EDGE",EDGE,{"derivedFrom":[subQ4,makeQuery(id+"F23.imprint","IMPRINT",EDGE,{"disambiguationData":[TD([[subQ7,1.0]])],"derivedFrom":subQ6})]})}),makeQuery(id+"F25.opExtrude","TWEAK_EDGE",EDGE,{"derivedFrom":[makeQuery(id+"F23.imprint","IMPRINT",EDGE,{"disambiguationData":[TD([[makeQuery(id+"F23.imprint","INTERSECT",VERTEX,{"derivedFrom":[subQ6,sQuery(id+"F23.wireOp",EDGE,"E38")]}),1.0]])],"derivedFrom":subQ6}),subQ5]}),makeQuery(id+"F25.opExtrude","TWEAK_EDGE",EDGE,{"derivedFrom":[makeQuery(id+"F24.boolean.opBoolean","COPY",EDGE,{"derivedFrom":makeQuery(id+"F24.opExtrude","CAP_EDGE",EDGE,{"disambiguationData":[OSD([subQ6])],"isStart":true})}),subQ5]})]});}
            var Q3;
            {var subQ0=sQuery(id+"F23.wireOp",EDGE,"E37");var subQ1=makeQuery(id+"F24.boolean.opBoolean","COPY",EDGE,{"derivedFrom":makeQuery(id+"F24.opExtrude","CAP_EDGE",EDGE,{"disambiguationData":[OSD([subQ0])],"isStart":true})});Q3=makeQuery(id+"F25.boolean.opBoolean","MERGE",EDGE,{"derivedFrom":[subQ1,makeQuery(id+"F25.opExtrude","CAP_EDGE",EDGE,{"disambiguationData":[OSD([subQ0]),TDD([makeQuery(id+"F23.imprint","IMPRINT",EDGE,{"disambiguationData":[TD([[makeQuery(id+"F23.imprint","INTERSECT",VERTEX,{"derivedFrom":[subQ0,sQuery(id+"F23.wireOp",EDGE,"E38")]}),1.0]])],"derivedFrom":subQ0})])],"isStart":true}),makeQuery(id+"F25.opExtrude","CAP_EDGE",EDGE,{"disambiguationData":[OSD([subQ0]),TDD([subQ1])],"isStart":true})]});}
            var Q4;
            Q4=makeQuery(id+"F19.opPattern","COPY",EDGE,{"derivedFrom":makeQuery(id+"F10.opExtrude","CAP_EDGE",EDGE,{"disambiguationData":[OSD([sQuery(id+"F7.wireOp",EDGE,"E13"),sQuery(id+"F7.wireOp",EDGE,"E22")])],"isStart":false}),"instanceName":"1"});
            var Q5;
            Q5=makeQuery(id+"F19.opPattern","COPY",EDGE,{"derivedFrom":makeQuery(id+"F10.opExtrude","CAP_EDGE",EDGE,{"disambiguationData":[OSD([sQuery(id+"F7.wireOp",EDGE,"E0")])],"isStart":false}),"instanceName":"1"});
            var Q6;
            Q6=makeQuery(id+"F19.opPattern","COPY",EDGE,{"derivedFrom":makeQuery(id+"F10.opExtrude","CAP_EDGE",EDGE,{"disambiguationData":[OSD([sQuery(id+"F7.wireOp",EDGE,"E1")])],"isStart":false}),"instanceName":"1"});
            var Q7;
            Q7=makeQuery(id+"F19.opPattern","COPY",EDGE,{"derivedFrom":makeQuery(id+"F10.opExtrude","CAP_EDGE",EDGE,{"disambiguationData":[OSD([sQuery(id+"F7.wireOp",EDGE,"E3")])],"isStart":false}),"instanceName":"1"});
            var Q8;
            Q8=makeQuery(id+"F19.opPattern","COPY",EDGE,{"derivedFrom":makeQuery(id+"F10.opExtrude","CAP_EDGE",EDGE,{"disambiguationData":[OSD([sQuery(id+"F7.wireOp",EDGE,"E2")])],"isStart":false}),"instanceName":"1"});
            var Q9;
            Q9=makeQuery(id+"F19.opPattern","COPY",EDGE,{"derivedFrom":makeQuery(id+"F10.opExtrude","CAP_EDGE",EDGE,{"disambiguationData":[OSD([sQuery(id+"F7.wireOp",EDGE,"E4")])],"isStart":false}),"instanceName":"1"});
            var Q10;
            Q10=makeQuery(id+"F19.opPattern","COPY",EDGE,{"derivedFrom":makeQuery(id+"F10.opExtrude","CAP_EDGE",EDGE,{"disambiguationData":[OSD([sQuery(id+"F7.wireOp",EDGE,"E5")])],"isStart":false}),"instanceName":"1"});
            var Q11;
            Q11=makeQuery(id+"F19.opPattern","COPY",FACE,{"derivedFrom":makeQuery(id+"F9.opExtrude","CAP_FACE",FACE,{"disambiguationData":[OSD([sQuery(id+"F7.wireOp",EDGE,"E0"),sQuery(id+"F7.wireOp",EDGE,"E1"),sQuery(id+"F7.wireOp",EDGE,"E2"),sQuery(id+"F7.wireOp",EDGE,"E3"),sQuery(id+"F7.wireOp",EDGE,"E4"),sQuery(id+"F7.wireOp",EDGE,"E5"),sQuery(id+"F7.wireOp",EDGE,"E20"),sQuery(id+"F7.wireOp",EDGE,"E21"),sQuery(id+"F7.wireOp",EDGE,"E22"),sQuery(id+"F7.wireOp",EDGE,"E23"),sQuery(id+"F7.wireOp",EDGE,"E24.filletArc")])],"isStart":false}),"instanceName":"1"});
            var Q12;
            Q12=makeQuery(id+"F9.opExtrude","CAP_FACE",FACE,{"disambiguationData":[OSD([sQuery(id+"F7.wireOp",EDGE,"E0"),sQuery(id+"F7.wireOp",EDGE,"E1"),sQuery(id+"F7.wireOp",EDGE,"E2"),sQuery(id+"F7.wireOp",EDGE,"E3"),sQuery(id+"F7.wireOp",EDGE,"E4"),sQuery(id+"F7.wireOp",EDGE,"E5"),sQuery(id+"F7.wireOp",EDGE,"E20"),sQuery(id+"F7.wireOp",EDGE,"E21"),sQuery(id+"F7.wireOp",EDGE,"E22"),sQuery(id+"F7.wireOp",EDGE,"E23"),sQuery(id+"F7.wireOp",EDGE,"E24.filletArc")])],"isStart":false});
            var Q13;
            {var subQ0=sQuery(id+"F7.wireOp",EDGE,"E3");Q13=makeQuery(id+"F19.opPattern","COPY",FACE,{"derivedFrom":makeQuery(id+"F10.boolean.opBoolean","MERGE",FACE,{"derivedFrom":[makeQuery(id+"F9.boolean.opBoolean","MERGE",FACE,{"derivedFrom":[makeQuery(id+"F8.opExtrude","SWEPT_FACE",FACE,{"disambiguationData":[OSD([subQ0])]}),makeQuery(id+"F9.opExtrude","SWEPT_FACE",FACE,{"disambiguationData":[OSD([subQ0])]})]}),makeQuery(id+"F10.opExtrude","SWEPT_FACE",FACE,{"disambiguationData":[OSD([subQ0])]})]}),"instanceName":"1"});}
            var Q14;
            {var subQ0=sQuery(id+"F7.wireOp",EDGE,"E3");Q14=makeQuery(id+"F10.boolean.opBoolean","MERGE",FACE,{"derivedFrom":[makeQuery(id+"F9.boolean.opBoolean","MERGE",FACE,{"derivedFrom":[makeQuery(id+"F8.opExtrude","SWEPT_FACE",FACE,{"disambiguationData":[OSD([subQ0])]}),makeQuery(id+"F9.opExtrude","SWEPT_FACE",FACE,{"disambiguationData":[OSD([subQ0])]})]}),makeQuery(id+"F10.opExtrude","SWEPT_FACE",FACE,{"disambiguationData":[OSD([subQ0])]})]});}
            chamfer(context, id + "F32", {"entities" : qUnion([Q0, Q1, Q2, Q3, Q4, Q5, Q6, Q7, Q8, Q9, Q10, Q11, Q12, Q13, Q14]), "width" : 1 * mm, "tangentPropagation" : true});
        }
    });
